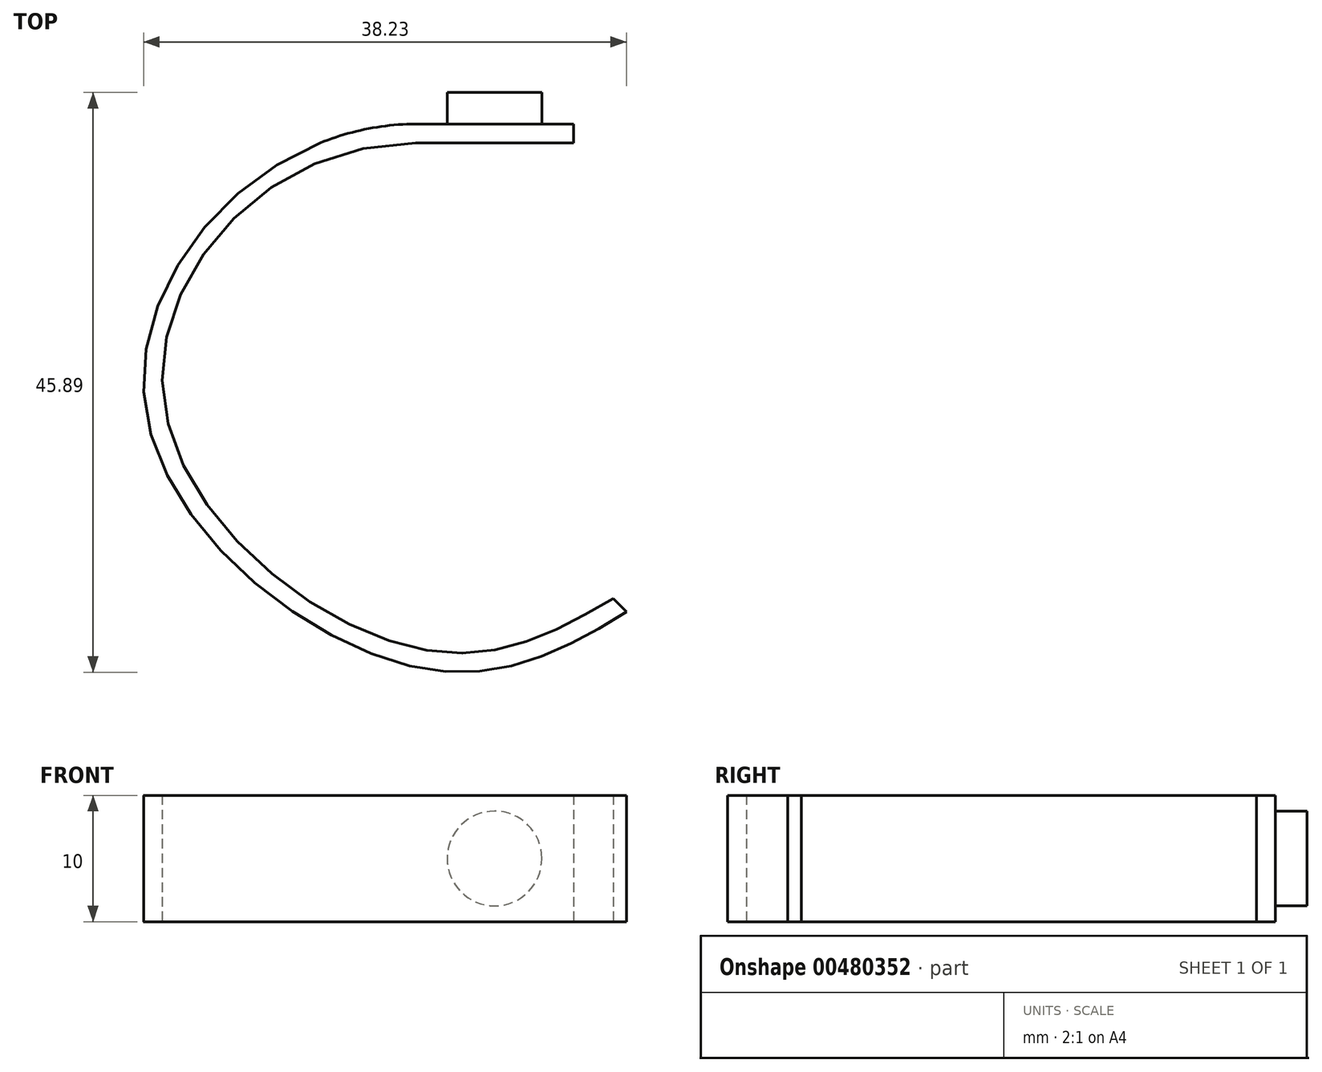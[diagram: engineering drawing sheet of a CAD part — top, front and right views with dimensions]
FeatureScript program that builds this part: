
annotation { "Feature Type Name" : "Feature", "Feature Type Description" : "" }
export const myFeature = defineFeature(function(context is Context, id is Id, definition is map)
    precondition{}
    {
        {
            var Q0;
            Q0=qCreatedBy(makeId("Top.planeOp"),FACE);
            var sketch = newSketch(context, id + "F0", { "sketchPlane" : qUnion([Q0])});
            skLineSegment(sketch, "E0", {"start": v(0, 0) * mm, "end": v(-20, 0) * mm, "construction": true});
            skLineSegment(sketch, "E1", {"start": v(-20, 0) * mm, "end": v(20, 0) * mm, "construction": true});
            skLineSegment(sketch, "E2", {"start": v(0, 0) * mm, "end": v(0, -20) * mm, "construction": true});
            skLineSegment(sketch, "E3", {"start": v(0, 0) * mm, "end": v(15.65, -16.05) * mm, "construction": true});
            skLineSegment(sketch, "E4", {"start": v(0, 0) * mm, "end": v(0, 20) * mm, "construction": true});
            skFitSpline(sketch, "E5", {"points": [v(15.65, -16.05) * mm, v(0, -20) * mm, v(-20, 0) * mm, v(0, 20) * mm], "startDerivative": vector(-51.15, -30.51) * mm, "endDerivative": vector(99.2, 0) * mm});
            skLineSegment(sketch, "E6", {"start": v(15.65, -16.05) * mm, "end": v(16.7, -17.12) * mm});
            skLineSegment(sketch, "E7", {"start": v(0, -20) * mm, "end": v(0, -21.5) * mm, "construction": true});
            skLineSegment(sketch, "E8", {"start": v(-20, 0) * mm, "end": v(-21.5, 0) * mm, "construction": true});
            skLineSegment(sketch, "E9", {"start": v(0, 20) * mm, "end": v(0, 21.5) * mm});
            skFitSpline(sketch, "E10", {"points": [v(16.7, -17.12) * mm, v(0, -21.5) * mm, v(-21.5, 0) * mm, v(0, 21.5) * mm], "startDerivative": vector(-54.58, -33.39) * mm, "endDerivative": vector(99.12, 0) * mm});
            skLineSegment(sketch, "E11", {"start": v(0, 21.5) * mm, "end": v(-12, 21.5) * mm, "construction": true});
            skLineSegment(sketch, "E12", {"start": v(0, 20) * mm, "end": v(-12, 20) * mm});
            skLineSegment(sketch, "E13.bottom", {"start": v(0, 21.5) * mm, "end": v(12.5, 21.5) * mm});
            skLineSegment(sketch, "E13.top", {"start": v(0, 20) * mm, "end": v(12.5, 20) * mm});
            skLineSegment(sketch, "E13.left", {"start": v(0, 21.5) * mm, "end": v(0, 20) * mm});
            skLineSegment(sketch, "E13.right", {"start": v(12.5, 21.5) * mm, "end": v(12.5, 20) * mm});
            skSolve(sketch);
        }
        {
            var Q0;
            Q0 = qSketchRegion(id + "F0", true);
            extrude(context, id + "F1", {"entities" : qUnion([Q0]), "depth" : 10 * mm});
        }
        {
            var Q0;
            Q0=makeQuery(id+"F1.opExtrude","SWEPT_FACE",FACE,{"disambiguationData":[OSD([sQuery(id+"F0.wireOp",EDGE,"E13.bottom")])]});
            var sketch = newSketch(context, id + "F2", { "sketchPlane" : qUnion([Q0])});
            skLineSegment(sketch, "E14", {"start": v(-6.25, 10) * mm, "end": v(-6.25, 5) * mm, "construction": true});
            skPoint(sketch, "E14.endSnap0", {"position": v(-6.25, 0) * mm});
            skCircle(sketch, "E15", {"center": v(-6.25, 5) * mm, "radius": 3.75 * mm});
            skSolve(sketch);
        }
        {
            var Q0;
            Q0 = qSketchRegion(id + "F2", true);
            extrude(context, id + "F3", {"entities" : qUnion([Q0]), "operationType" : NewBodyOperationType.ADD, "depth" : 2.5 * mm});
        }
    });
